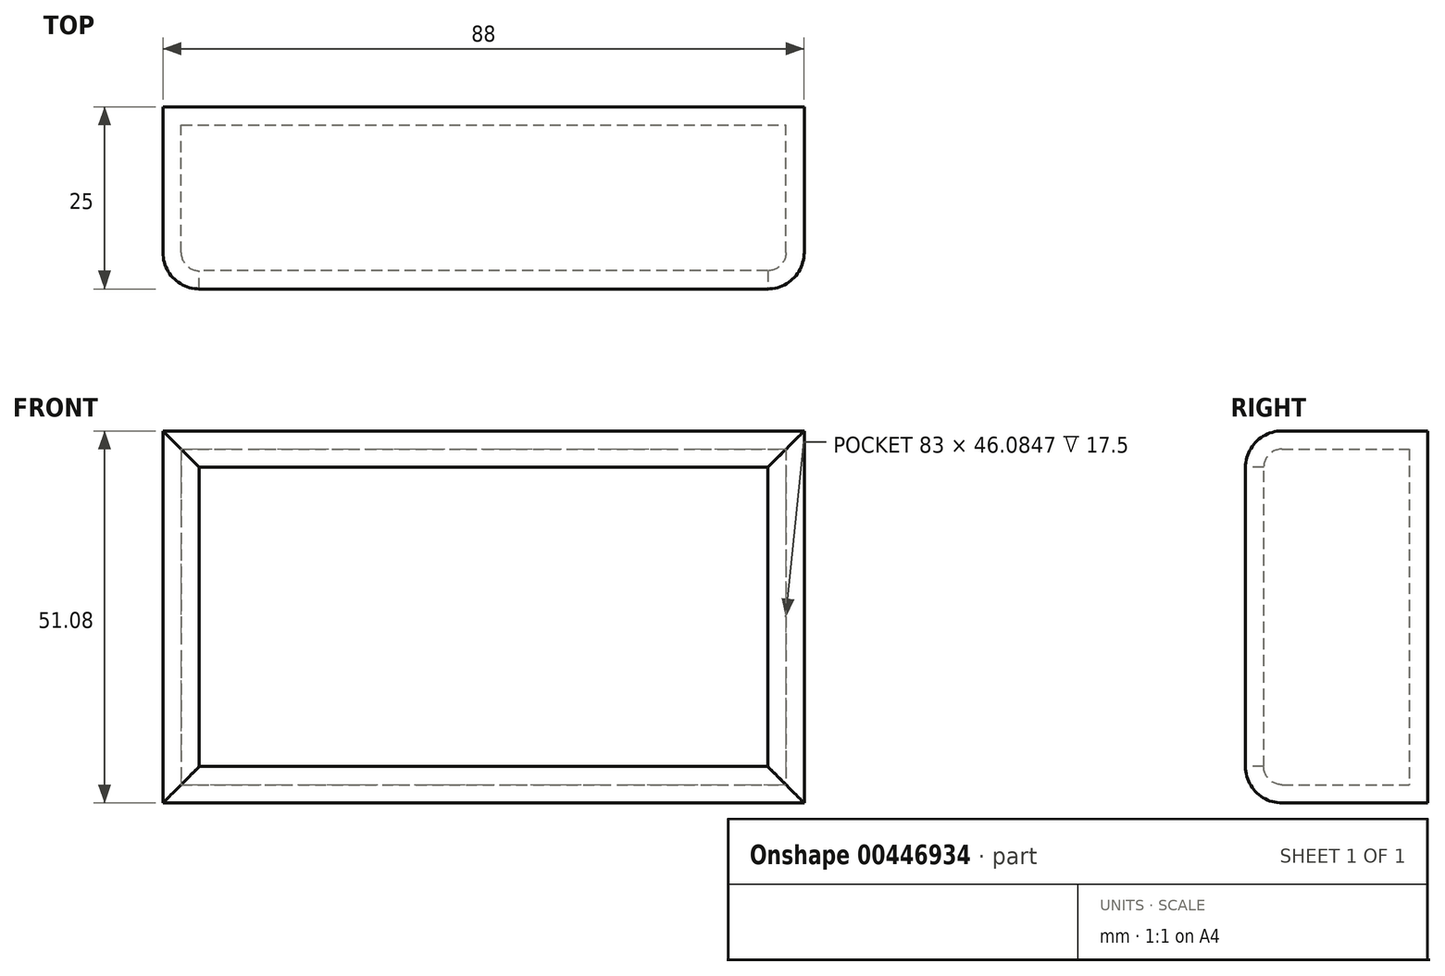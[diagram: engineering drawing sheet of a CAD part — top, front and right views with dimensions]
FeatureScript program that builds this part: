
annotation { "Feature Type Name" : "Feature", "Feature Type Description" : "" }
export const myFeature = defineFeature(function(context is Context, id is Id, definition is map)
    precondition{}
    {
        {
            var Q0;
            Q0=qCreatedBy(makeId("Front.planeOp"),FACE);
            var sketch = newSketch(context, id + "F0", { "sketchPlane" : qUnion([Q0])});
            skLineSegment(sketch, "E0.bottom", {"start": v(-52.02, 51.08) * mm, "end": v(35.98, 51.08) * mm});
            skLineSegment(sketch, "E0.top", {"start": v(-52.02, 0) * mm, "end": v(35.98, 0) * mm});
            skLineSegment(sketch, "E0.left", {"start": v(-52.02, 51.08) * mm, "end": v(-52.02, 0) * mm});
            skLineSegment(sketch, "E0.right", {"start": v(35.98, 51.08) * mm, "end": v(35.98, 0) * mm});
            skSolve(sketch);
        }
        {
            var Q0;
            Q0=makeQuery(id+"F0.imprint","IMPRINT",FACE,{"disambiguationData":[TD([[makeQuery(id+"F0.imprint","IMPRINT",EDGE,{"derivedFrom":sQuery(id+"F0.wireOp",EDGE,"E0.bottom")}),-1.0]])]});
            extrude(context, id + "F1", {"entities" : qUnion([Q0]), "depth" : 25 * mm});
        }
        {
            var Q0;
            Q0=makeQuery(id+"F1.opExtrude","CAP_EDGE",EDGE,{"disambiguationData":[OSD([sQuery(id+"F0.wireOp",EDGE,"E0.left")])],"isStart":false});
            var Q1;
            Q1=makeQuery(id+"F1.opExtrude","CAP_EDGE",EDGE,{"disambiguationData":[OSD([sQuery(id+"F0.wireOp",EDGE,"E0.top")])],"isStart":false});
            var Q2;
            Q2=makeQuery(id+"F1.opExtrude","CAP_EDGE",EDGE,{"disambiguationData":[OSD([sQuery(id+"F0.wireOp",EDGE,"E0.right")])],"isStart":false});
            var Q3;
            Q3=makeQuery(id+"F1.opExtrude","CAP_EDGE",EDGE,{"disambiguationData":[OSD([sQuery(id+"F0.wireOp",EDGE,"E0.bottom")])],"isStart":false});
            fillet(context, id + "F2", {"entities" : qUnion([Q0, Q1, Q2, Q3]), "radius" : 5 * mm, "tangentPropagation" : true, "allowEdgeOverflow" : false});
        }
        {
            var Q0;
            Q0=makeQuery(id+"F1.opExtrude","CAP_FACE",FACE,{"disambiguationData":[OSD([sQuery(id+"F0.wireOp",EDGE,"E0.bottom"),sQuery(id+"F0.wireOp",EDGE,"E0.top"),sQuery(id+"F0.wireOp",EDGE,"E0.left"),sQuery(id+"F0.wireOp",EDGE,"E0.right")])],"isStart":false});
            shell(context, id + "F3", {"entities" : qUnion([Q0]), "thickness" : 2.5 * mm});
        }
    });
